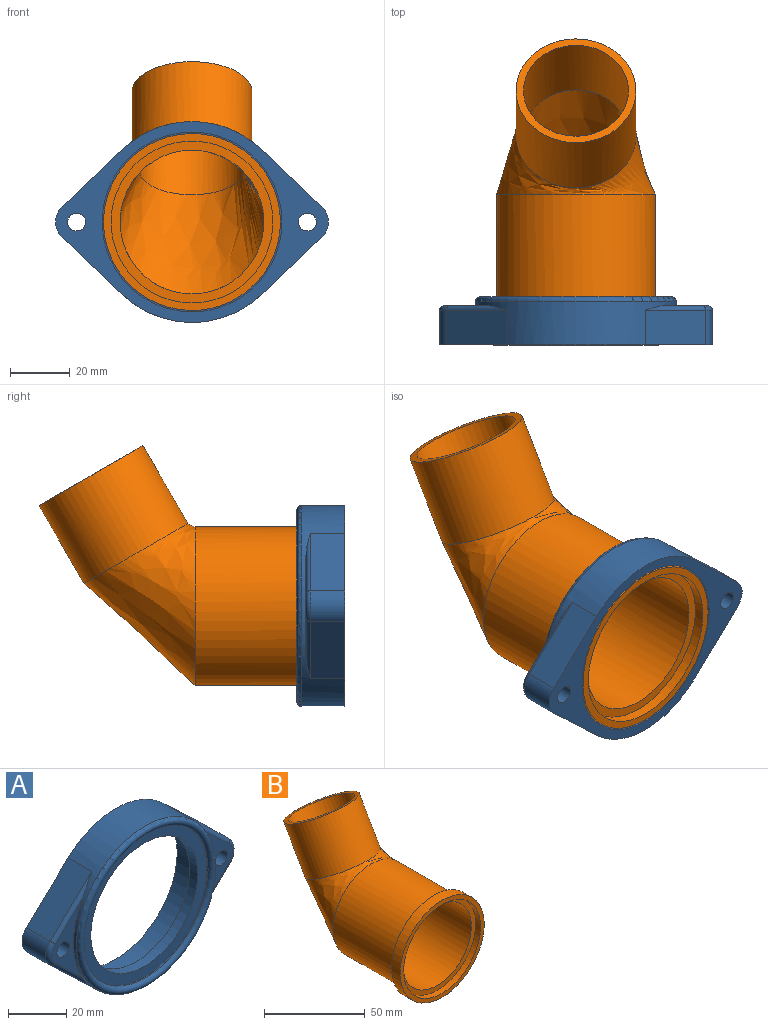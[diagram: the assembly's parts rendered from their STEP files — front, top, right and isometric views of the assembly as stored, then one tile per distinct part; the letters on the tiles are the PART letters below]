
ASSEMBLY  parts=2 mates=1
PART A: 24 faces, bbox 92.2x16x72.5 mm
  f0: plane 32.78x14.78mm, normal (0,-1,0), area 152.7mm2, adj f6,f11,f19,f20,f21
  f1: cylinder r=7mm len=11.5mm, axis (0,-1,0), area 130.7mm2, adj f2,f7,f9,f20
  f2: plane 20.26x19.22mm, normal (0.69,0,0.73), area 321.2mm2, adj f1,f6,f9,f21
  f3: plane 20.26x19.22mm, normal (-0.69,0,0.73), area 321.2mm2, adj f4,f6,f9,f16
  f4: cylinder r=7mm len=11.5mm, axis (0,-1,0), area 130.7mm2, adj f3,f5,f9,f17
  f5: plane 20.26x19.22mm, normal (-0.69,0,-0.73), area 321.2mm2, adj f4,f6,f9,f18
  f6: cylinder r=33.5mm len=67mm, axis (0,-1,0), area 1661.7mm2, adj f0,f2,f3,f5,f7,f8,f9,f14
  f7: plane 20.26x19.22mm, normal (0.69,0,-0.73), area 321.2mm2, adj f1,f6,f9,f19
  f8: plane 32.78x14.78mm, normal (0,-1,0), area 152.7mm2, adj f6,f10,f16,f17,f18
  f9: plane 91x67mm, normal (0,1,0), area 1161.7mm2, adj f1,f2,f3,f4,f5,f6,f7,f10
  f10: cylinder r=3mm len=13mm, axis (0,-1,0), area 245mm2, adj f8,f9
  f11: cylinder r=3mm len=13mm, axis (0,-1,0), area 245mm2, adj f0,f9
  f12: cylinder r=26mm len=52mm, axis (0,-1,0), area 653.5mm2, adj f15,f23
  f13: cylinder r=30.5mm len=61mm, axis (0,1,0), area 95.8mm2, adj f14,f15
  f14: torus R=32mm, axis (0,-1,0), area 947.5mm2, adj f6,f13
  f15: plane 61x61mm, normal (0,-1,0), area 798.7mm2, adj f12,f13
  f16: cylinder r=1.5mm len=21.29mm, axis (-0.73,0,-0.69), area 53.4mm2, adj f3,f6,f8,f17
  f17: torus R=5.5mm, axis (0,-1,0), area 24.7mm2, adj f4,f8,f16,f18
  f18: cylinder r=1.5mm len=21.29mm, axis (0.73,0,-0.69), area 53.4mm2, adj f5,f6,f8,f17
  f19: cylinder r=1.5mm len=21.29mm, axis (0.73,0,0.69), area 53.4mm2, adj f0,f6,f7,f20
  f20: torus R=5.5mm, axis (0,-1,0), area 24.7mm2, adj f0,f1,f19,f21
  f21: cylinder r=1.5mm len=21.29mm, axis (-0.73,0,0.69), area 53.4mm2, adj f0,f2,f6,f20
  f22: cylinder r=30mm len=60mm, axis (0,1,0), area 1885mm2, adj f9,f23
  f23: plane 60x60mm, normal (0,1,0), area 703.7mm2, adj f12,f22
PART B: 12 faces, bbox 64x107x88 mm
  f0: cylinder r=26.5mm len=53mm, axis (0,-1,0), area 7326.2mm2, adj f2,f6
  f1: cylinder r=29.5mm len=59mm, axis (0,-1,0), area 1112.1mm2, adj f2,f3
  f2: plane 59x59mm, normal (0,1,0), area 527.8mm2, adj f0,f1
  f3: plane 59x59mm, normal (0,-1,0), area 443.7mm2, adj f1,f8
  f4: cylinder r=20mm len=49.64mm, axis (0,-0.5,-0.87), area 3769.9mm2, adj f5,f6
  f5: plane 40x34.64mm, normal (0,0.5,0.87), area 294.5mm2, adj f4,f10
  f6: bspline ~56.95x54.14mm, area 3575.7mm2, adj f0,f4
  f7: cylinder r=24mm len=48mm, axis (0,-1,0), area 6891.9mm2, adj f9,f11
  f8: cylinder r=27mm len=54mm, axis (0,-1,0), area 593.8mm2, adj f3,f9
  f9: plane 54x54mm, normal (0,-1,0), area 480.7mm2, adj f7,f8
  f10: cylinder r=17.5mm len=45.66mm, axis (0,-0.5,-0.87), area 3316.4mm2, adj f5,f11
  f11: offset ~61.72x58.98mm, area 3196mm2, adj f7,f10
PLACE A rot(axis=(1,0,0),180deg) t=(0,0,0)mm
PLACE B at identity
MATE fastened A.f12 <-> B.f0  axis (0,-1,0) through (0,0,0)mm
